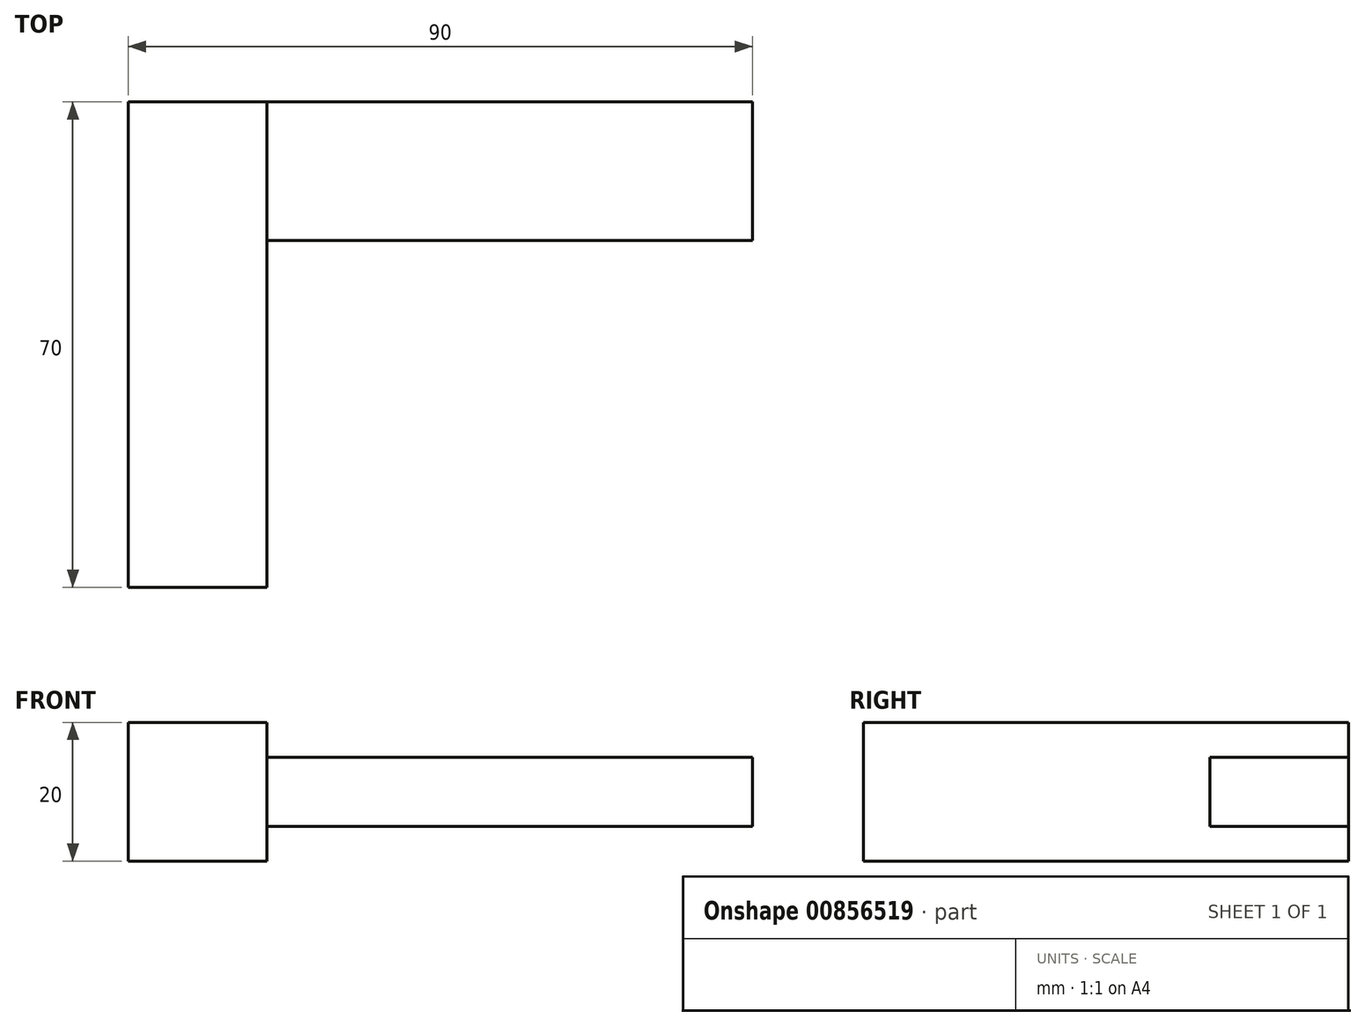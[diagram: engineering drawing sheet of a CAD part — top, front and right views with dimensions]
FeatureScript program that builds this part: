
annotation { "Feature Type Name" : "Feature", "Feature Type Description" : "" }
export const myFeature = defineFeature(function(context is Context, id is Id, definition is map)
    precondition{}
    {
        {
            var Q0;
            Q0=qCreatedBy(makeId("Top.planeOp"),FACE);
            var sketch = newSketch(context, id + "F0", { "sketchPlane" : qUnion([Q0])});
            skLineSegment(sketch, "E0.bottom", {"start": v(-10, 35) * mm, "end": v(10, 35) * mm});
            skLineSegment(sketch, "E0.top", {"start": v(-10, -35) * mm, "end": v(10, -35) * mm});
            skLineSegment(sketch, "E0.left", {"start": v(-10, 35) * mm, "end": v(-10, -35) * mm});
            skLineSegment(sketch, "E0.right", {"start": v(10, 35) * mm, "end": v(10, -35) * mm});
            skPoint(sketch, "E0.middle", {"position": v(0, 0) * mm});
            skSolve(sketch);
        }
        {
            var Q0;
            Q0=makeQuery(id+"F0.imprint","IMPRINT",FACE,{"disambiguationData":[TD([[makeQuery(id+"F0.imprint","IMPRINT",EDGE,{"derivedFrom":sQuery(id+"F0.wireOp",EDGE,"E0.bottom")}),-1.0]])]});
            extrude(context, id + "F1", {"entities" : qUnion([Q0]), "depth" : 20 * mm, "offsetDistance" : 25 * mm});
        }
        {
            var Q0;
            Q0=makeQuery(id+"F1.opExtrude","SWEPT_FACE",FACE,{"disambiguationData":[OSD([sQuery(id+"F0.wireOp",EDGE,"E0.right")])]});
            var sketch = newSketch(context, id + "F2", { "sketchPlane" : qUnion([Q0])});
            skLineSegment(sketch, "E1", {"start": v(35, 10) * mm, "end": v(35, 15) * mm, "construction": true});
            skLineSegment(sketch, "E2.bottom", {"start": v(35, 15) * mm, "end": v(15, 15) * mm});
            skLineSegment(sketch, "E2.top", {"start": v(35, 5) * mm, "end": v(15, 5) * mm});
            skLineSegment(sketch, "E2.left", {"start": v(35, 15) * mm, "end": v(35, 5) * mm});
            skLineSegment(sketch, "E2.right", {"start": v(15, 15) * mm, "end": v(15, 5) * mm});
            skSolve(sketch);
        }
        {
            var Q0;
            Q0=makeQuery(id+"F2.imprint","IMPRINT",FACE,{"disambiguationData":[TD([[makeQuery(id+"F2.imprint","IMPRINT",EDGE,{"derivedFrom":sQuery(id+"F2.wireOp",EDGE,"E2.bottom")}),1.0]])]});
            extrude(context, id + "F3", {"entities" : qUnion([Q0]), "operationType" : NewBodyOperationType.ADD, "depth" : 70 * mm, "offsetDistance" : 25 * mm});
        }
    });
